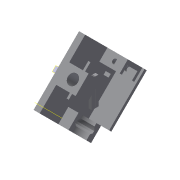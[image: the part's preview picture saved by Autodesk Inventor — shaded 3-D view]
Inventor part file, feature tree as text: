
AUTODESK INVENTOR PART (.ipt)
format: ipt  version: 2019.4 (Build 234330000, 330)  size: 266,240 bytes
history: native  units: mm
features: sketch x10, extrude x9, reference x9, plane x5, other x5, projected_geometry x4, revolve x1
ambient origin geometry x8: Origin, YZ Plane, XZ Plane, XY Plane, X Axis, Y Axis, Z Axis, Center Point
bodies: Solid1 (feature_tree)
feature tree (43):
  plane  "Work Plane1"
  plane  "Work Plane2"
  extrude  "Extrusion1"  Depth=42.0mm
  sketch  "Sketch2"  dims[d2=4.0mm d3=0.0mm d4=6.0mm]
  plane  "Work Plane3"
  extrude  "Extrusion2"  Depth=6.0mm
  sketch  "Sketch3"  dims[d5=6.0mm d6=6.0mm]
  sketch  "Sketch4"  dims[d7=0.3mm d8=4.0mm d9=0.0mm]
  plane  "Work Plane4"
  extrude  "Extrusion3"  Depth=6.0mm
  extrude  "Extrusion4"  Depth=4.0mm TaperAngle=0.0deg
  extrude  "Extrusion5"  Depth=2.0mm
  extrude  "Extrusion6"  Depth=2.0mm TaperAngle=0.0deg
  plane  "Work Plane5"
  extrude  "Extrusion7"  Depth=2.0mm
  revolve  "Revolution1"  [1 undecoded]
  extrude  "Extrusion8"  Depth=2.0mm
  extrude  "Extrusion9"  Depth=2.0mm TaperAngle=0.0deg
  sketch  "Sketch1"  dims[d0=38.0mm d1=42.0mm]
  reference  "Reference1"
  reference  "Reference2"
  reference  "Reference3"
  reference  "Reference4"
  projected_geometry  "Projected Loop1"
  reference  "Reference5"
  sketch  "Sketch5"  dims[d10=2.0mm d11=2.0mm]
  projected_geometry  "Projected Loop2"
  reference  "Reference6"
  reference  "Reference7"
  sketch  "Sketch6"  dims[d12=0.3mm d13=2.0mm d14=0.0mm]
  reference  "Reference8"
  sketch  "Sketch7"  dims[d15=5.0mm d16=2.0mm]
  reference  "Reference9"
  sketch  "Sketch8"  dims[d17=5.0mm d18=2.0mm]
  sketch  "Sketch9"  dims[d19=2.0mm d20=0.0mm d21=2.9mm]
  projected_geometry  "Projected Loop3"
  sketch  "Sketch10"  dims[d22=2.0mm d23=0.0mm d24=2.0mm d25=0.0mm d26=-3.25mm d27=3.25mm d28=6.0mm d29=0.0mm d30=0.0mm d32=90.0deg d33=2.0mm d34=8.0mm d35=0.0mm d36=20.0mm d37=2.0mm d38=3.25mm d39=0.0mm d40=10.0mm d41=2.0mm]
  projected_geometry  "Projected Loop4"
  other  "Assembly_Opentrons_Autofocus_Astigmatism_v0.iam"
  other  "00_ESP32_Camera_only:1"
  other  "00_IR_Laserdiode:1"
  other  "00_coverslip:1"
  other  "00_lens_10mm:1"
note: 1 required parameter value undecoded (feature->parameter linkage not recoverable at this tier; creation-order binding heuristic only, values carry confidence <= 0.55)
